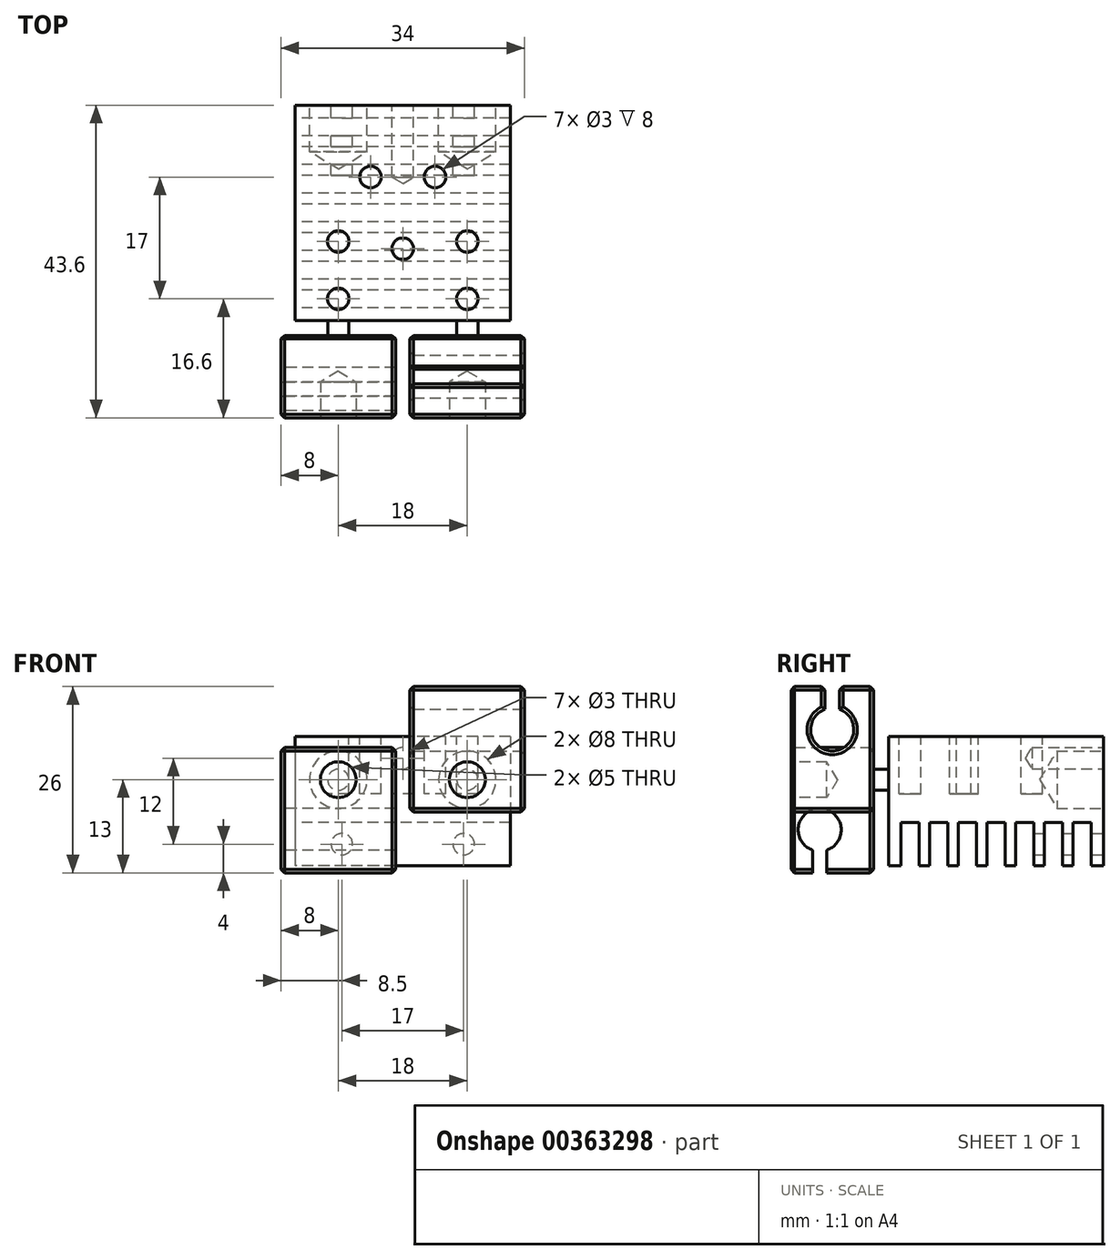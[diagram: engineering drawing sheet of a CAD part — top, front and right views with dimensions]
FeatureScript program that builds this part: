
annotation { "Feature Type Name" : "Feature", "Feature Type Description" : "" }
export const myFeature = defineFeature(function(context is Context, id is Id, definition is map)
    precondition{}
    {
        {
            var Q0;
            Q0=qCreatedBy(makeId("Top.planeOp"),FACE);
            var sketch = newSketch(context, id + "F0", { "sketchPlane" : qUnion([Q0])});
            skLineSegment(sketch, "E0.bottom", {"start": v(15, -15) * mm, "end": v(-15, -15) * mm});
            skLineSegment(sketch, "E0.top", {"start": v(15, 15) * mm, "end": v(-15, 15) * mm});
            skLineSegment(sketch, "E0.left", {"start": v(15, -15) * mm, "end": v(15, 15) * mm});
            skLineSegment(sketch, "E0.right", {"start": v(-15, -15) * mm, "end": v(-15, 15) * mm});
            skPoint(sketch, "E0.middle", {"position": v(0, 0) * mm});
            skSolve(sketch);
        }
        {
            var Q0;
            Q0=makeQuery(id+"F0.imprint","IMPRINT",FACE,{"disambiguationData":[TD([[makeQuery(id+"F0.imprint","IMPRINT",EDGE,{"derivedFrom":sQuery(id+"F0.wireOp",EDGE,"E0.bottom")}),-1.0]])]});
            extrude(context, id + "F11", {"entities" : qUnion([Q0]), "depth" : 18 * mm});
        }
        {
            var Q0;
            Q0=makeQuery(id+"F11.opExtrude","SWEPT_FACE",FACE,{"disambiguationData":[OSD([sQuery(id+"F0.wireOp",EDGE,"E0.top")])]});
            var sketch = newSketch(context, id + "F12", { "sketchPlane" : qUnion([Q0])});
            skPoint(sketch, "E1", {"position": v(-8.5, 3) * mm});
            skPoint(sketch, "E2", {"position": v(8.5, 3) * mm});
            skPoint(sketch, "E3", {"position": v(-9, 12) * mm});
            skPoint(sketch, "E4", {"position": v(9, 12) * mm});
            skPoint(sketch, "E5", {"position": v(0, 15) * mm});
            skSolve(sketch);
        }
        {
            var Q0;
            Q0=sQuery(id+"F12.wireOp",VERTEX,"E3");
            var Q1;
            Q1=sQuery(id+"F12.wireOp",VERTEX,"E4");
            var Q2;
            Q2=makeQuery(id+"F11.opExtrude","SWEPT_BODY",BODY,{"disambiguationData":[OSD([sQuery(id+"F0.wireOp",EDGE,"E0.bottom"),sQuery(id+"F0.wireOp",EDGE,"E0.top"),sQuery(id+"F0.wireOp",EDGE,"E0.left"),sQuery(id+"F0.wireOp",EDGE,"E0.right")])]});
            hole(context, id + "F1", {"style" : HoleStyle.SIMPLE, "endStyle" : HoleEndStyle.BLIND, "holeDiameter" : 8 * mm, "holeDepth" : 6.5 * mm, "locations" : qUnion([Q0, Q1]), "scope" : qUnion([Q2]), "tappedDepth" : 12 * mm, "tapClearance" : 3});
        }
        {
            var Q0;
            Q0=makeQuery(id+"F11.opExtrude","CAP_FACE",FACE,{"disambiguationData":[OSD([sQuery(id+"F0.wireOp",EDGE,"E0.bottom"),sQuery(id+"F0.wireOp",EDGE,"E0.top"),sQuery(id+"F0.wireOp",EDGE,"E0.left"),sQuery(id+"F0.wireOp",EDGE,"E0.right")])],"isStart":true});
            var sketch = newSketch(context, id + "F13", { "sketchPlane" : qUnion([Q0])});
            skLineSegment(sketch, "E6.bottom", {"start": v(15, -13.25) * mm, "end": v(-15.01, -13.25) * mm});
            skLineSegment(sketch, "E6.top", {"start": v(15, -10.75) * mm, "end": v(-15.01, -10.75) * mm});
            skLineSegment(sketch, "E6.left", {"start": v(15, -13.25) * mm, "end": v(15, -10.75) * mm});
            skLineSegment(sketch, "E6.right", {"start": v(-15.01, -13.25) * mm, "end": v(-15.01, -10.75) * mm});
            skLineSegment(sketch, "E7.0.1.0", {"start": v(15, -9.25) * mm, "end": v(15, -6.75) * mm});
            skLineSegment(sketch, "E7.0.1.1", {"start": v(-15.01, -9.25) * mm, "end": v(-15.01, -6.75) * mm});
            skLineSegment(sketch, "E7.0.1.2", {"start": v(15, -9.25) * mm, "end": v(-15.01, -9.25) * mm});
            skLineSegment(sketch, "E7.0.1.3", {"start": v(15, -6.75) * mm, "end": v(-15.01, -6.75) * mm});
            skLineSegment(sketch, "E7.0.2.0", {"start": v(15, -5.25) * mm, "end": v(15, -2.75) * mm});
            skLineSegment(sketch, "E7.0.2.1", {"start": v(-15.01, -5.25) * mm, "end": v(-15.01, -2.75) * mm});
            skLineSegment(sketch, "E7.0.2.2", {"start": v(15, -5.25) * mm, "end": v(-15.01, -5.25) * mm});
            skLineSegment(sketch, "E7.0.2.3", {"start": v(15, -2.75) * mm, "end": v(-15.01, -2.75) * mm});
            skLineSegment(sketch, "E7.0.3.0", {"start": v(15, -1.25) * mm, "end": v(15, 1.25) * mm});
            skLineSegment(sketch, "E7.0.3.1", {"start": v(-15.01, -1.25) * mm, "end": v(-15.01, 1.25) * mm});
            skLineSegment(sketch, "E7.0.3.2", {"start": v(15, -1.25) * mm, "end": v(-15.01, -1.25) * mm});
            skLineSegment(sketch, "E7.0.3.3", {"start": v(15, 1.25) * mm, "end": v(-15.01, 1.25) * mm});
            skLineSegment(sketch, "E7.0.4.0", {"start": v(15, 2.75) * mm, "end": v(15, 5.25) * mm});
            skLineSegment(sketch, "E7.0.4.1", {"start": v(-15.01, 2.75) * mm, "end": v(-15.01, 5.25) * mm});
            skLineSegment(sketch, "E7.0.4.2", {"start": v(15, 2.75) * mm, "end": v(-15.01, 2.75) * mm});
            skLineSegment(sketch, "E7.0.4.3", {"start": v(15, 5.25) * mm, "end": v(-15.01, 5.25) * mm});
            skLineSegment(sketch, "E7.0.5.0", {"start": v(15, 6.75) * mm, "end": v(15, 9.25) * mm});
            skLineSegment(sketch, "E7.0.5.1", {"start": v(-15.01, 6.75) * mm, "end": v(-15.01, 9.25) * mm});
            skLineSegment(sketch, "E7.0.5.2", {"start": v(15, 6.75) * mm, "end": v(-15.01, 6.75) * mm});
            skLineSegment(sketch, "E7.0.5.3", {"start": v(15, 9.25) * mm, "end": v(-15.01, 9.25) * mm});
            skLineSegment(sketch, "E7.0.6.0", {"start": v(15, 10.75) * mm, "end": v(15, 13.25) * mm});
            skLineSegment(sketch, "E7.0.6.1", {"start": v(-15.01, 10.75) * mm, "end": v(-15.01, 13.25) * mm});
            skLineSegment(sketch, "E7.0.6.2", {"start": v(15, 10.75) * mm, "end": v(-15.01, 10.75) * mm});
            skLineSegment(sketch, "E7.0.6.3", {"start": v(15, 13.25) * mm, "end": v(-15.01, 13.25) * mm});
            skLineSegment(sketch, "E7.direction1", {"start": v(-15.01, -13.25) * mm, "end": v(9.99, -13.25) * mm, "construction": true});
            skLineSegment(sketch, "E7.direction2", {"start": v(-15.01, -13.25) * mm, "end": v(-15.01, -9.25) * mm, "construction": true});
            skSolve(sketch);
        }
        {
            var Q0;
            {var subQ0=sQuery(id+"F13.wireOp",EDGE,"E7.0.6.0");Q0=makeQuery(id+"F13.imprint","IMPRINT",FACE,{"disambiguationData":[TD([[makeQuery(id+"F13.imprint","IMPRINT",EDGE,{"derivedFrom":subQ0}),-1.0]])]});}
            var Q1;
            {var subQ0=sQuery(id+"F13.wireOp",EDGE,"E7.0.5.0");Q1=makeQuery(id+"F13.imprint","IMPRINT",FACE,{"disambiguationData":[TD([[makeQuery(id+"F13.imprint","IMPRINT",EDGE,{"derivedFrom":subQ0}),-1.0]])]});}
            var Q2;
            {var subQ0=sQuery(id+"F13.wireOp",EDGE,"E7.0.4.0");Q2=makeQuery(id+"F13.imprint","IMPRINT",FACE,{"disambiguationData":[TD([[makeQuery(id+"F13.imprint","IMPRINT",EDGE,{"derivedFrom":subQ0}),-1.0]])]});}
            var Q3;
            {var subQ0=sQuery(id+"F13.wireOp",EDGE,"E7.0.3.0");Q3=makeQuery(id+"F13.imprint","IMPRINT",FACE,{"disambiguationData":[TD([[makeQuery(id+"F13.imprint","IMPRINT",EDGE,{"derivedFrom":subQ0}),-1.0]])]});}
            var Q4;
            {var subQ0=sQuery(id+"F13.wireOp",EDGE,"E7.0.2.0");Q4=makeQuery(id+"F13.imprint","IMPRINT",FACE,{"disambiguationData":[TD([[makeQuery(id+"F13.imprint","IMPRINT",EDGE,{"derivedFrom":subQ0}),-1.0]])]});}
            var Q5;
            {var subQ0=sQuery(id+"F13.wireOp",EDGE,"E7.0.1.0");Q5=makeQuery(id+"F13.imprint","IMPRINT",FACE,{"disambiguationData":[TD([[makeQuery(id+"F13.imprint","IMPRINT",EDGE,{"derivedFrom":subQ0}),-1.0]])]});}
            var Q6;
            {var subQ0=sQuery(id+"F13.wireOp",EDGE,"E6.left");Q6=makeQuery(id+"F13.imprint","IMPRINT",FACE,{"disambiguationData":[TD([[makeQuery(id+"F13.imprint","IMPRINT",EDGE,{"derivedFrom":subQ0}),-1.0]])]});}
            extrude(context, id + "F14", {"entities" : qUnion([Q0, Q1, Q2, Q3, Q4, Q5, Q6]), "operationType" : NewBodyOperationType.REMOVE, "oppositeDirection" : true, "depth" : 6 * mm});
        }
        {
            var Q0;
            Q0=sQuery(id+"F12.wireOp",VERTEX,"E2");
            var Q1;
            Q1=sQuery(id+"F12.wireOp",VERTEX,"E1");
            var Q2;
            Q2=sQuery(id+"F12.wireOp",VERTEX,"E5");
            var Q3;
            Q3=makeQuery(id+"F11.opExtrude","SWEPT_BODY",BODY,{"disambiguationData":[OSD([sQuery(id+"F0.wireOp",EDGE,"E0.bottom"),sQuery(id+"F0.wireOp",EDGE,"E0.top"),sQuery(id+"F0.wireOp",EDGE,"E0.left"),sQuery(id+"F0.wireOp",EDGE,"E0.right")])]});
            hole(context, id + "F15", {"style" : HoleStyle.SIMPLE, "endStyle" : HoleEndStyle.BLIND, "holeDiameter" : 3 * mm, "holeDepth" : 10 * mm, "locations" : qUnion([Q0, Q1, Q2]), "scope" : qUnion([Q3])});
        }
        {
            var Q0;
            Q0=makeQuery(id+"F11.opExtrude","SWEPT_FACE",FACE,{"disambiguationData":[OSD([sQuery(id+"F0.wireOp",EDGE,"E0.bottom")])]});
            var sketch = newSketch(context, id + "F2", { "sketchPlane" : qUnion([Q0])});
            skCircle(sketch, "E8", {"center": v(9, 12) * mm, "radius": 1.48 * mm});
            skCircle(sketch, "E9", {"center": v(-9, 12) * mm, "radius": 1.48 * mm});
            skLineSegment(sketch, "E10", {"start": v(-15, 12) * mm, "end": v(15, 12) * mm, "construction": true});
            skSolve(sketch);
        }
        {
            var Q0;
            Q0=makeQuery(id+"F2.imprint","IMPRINT",FACE,{"disambiguationData":[TD([[makeQuery(id+"F2.imprint","IMPRINT",EDGE,{"derivedFrom":sQuery(id+"F2.wireOp",EDGE,"E9")}),1.0]])]});
            var Q1;
            Q1=makeQuery(id+"F2.imprint","IMPRINT",FACE,{"disambiguationData":[TD([[makeQuery(id+"F2.imprint","IMPRINT",EDGE,{"derivedFrom":sQuery(id+"F2.wireOp",EDGE,"E8")}),1.0]])]});
            extrude(context, id + "F3", {"entities" : qUnion([Q0, Q1]), "operationType" : NewBodyOperationType.ADD, "depth" : 2.1 * mm});
        }
        {
            var Q0;
            Q0=makeQuery(id+"F3.opExtrude","CAP_FACE",FACE,{"disambiguationData":[OSD([sQuery(id+"F2.wireOp",EDGE,"E8")])],"isStart":false});
            var sketch = newSketch(context, id + "F16", { "sketchPlane" : qUnion([Q0])});
            skLineSegment(sketch, "E11.bottom", {"start": v(1, 25) * mm, "end": v(17, 25) * mm});
            skLineSegment(sketch, "E11.top", {"start": v(1, 7.5) * mm, "end": v(17, 7.5) * mm});
            skLineSegment(sketch, "E11.left", {"start": v(1, 25) * mm, "end": v(1, 7.5) * mm});
            skLineSegment(sketch, "E11.right", {"start": v(17, 25) * mm, "end": v(17, 7.5) * mm});
            skPoint(sketch, "E12", {"position": v(9, 12) * mm});
            skSolve(sketch);
        }
        {
            var Q0;
            Q0=makeQuery(id+"F3.opExtrude","CAP_FACE",FACE,{"disambiguationData":[OSD([sQuery(id+"F2.wireOp",EDGE,"E9")])],"isStart":false});
            var sketch = newSketch(context, id + "F17", { "sketchPlane" : qUnion([Q0])});
            skPoint(sketch, "E13", {"position": v(-9, 12) * mm});
            skLineSegment(sketch, "E14.bottom", {"start": v(-17, 16.5) * mm, "end": v(-1, 16.5) * mm});
            skLineSegment(sketch, "E14.top", {"start": v(-17, -1) * mm, "end": v(-1, -1) * mm});
            skLineSegment(sketch, "E14.left", {"start": v(-17, 16.5) * mm, "end": v(-17, -1) * mm});
            skLineSegment(sketch, "E14.right", {"start": v(-1, 16.5) * mm, "end": v(-1, -1) * mm});
            skSolve(sketch);
        }
        {
            var Q0;
            Q0=qSketchRegion(id+"F17",true);
            var Q1;
            Q1=qSketchRegion(id+"F16",true);
            extrude(context, id + "F18", {"entities" : qUnion([Q0, Q1]), "operationType" : NewBodyOperationType.ADD, "depth" : 11.5 * mm});
        }
        {
            var Q0;
            Q0=makeQuery(id+"F18.opExtrude","CAP_FACE",FACE,{"disambiguationData":[OSD([sQuery(id+"F16.wireOp",EDGE,"E11.bottom"),sQuery(id+"F16.wireOp",EDGE,"E11.top"),sQuery(id+"F16.wireOp",EDGE,"E11.left"),sQuery(id+"F16.wireOp",EDGE,"E11.right")])],"isStart":false});
            var sketch = newSketch(context, id + "F19", { "sketchPlane" : qUnion([Q0])});
            skPoint(sketch, "E15", {"position": v(9, 12) * mm});
            skPoint(sketch, "E15.positionSnap0", {"position": v(9, 7.5) * mm});
            skSolve(sketch);
        }
        {
            var Q0;
            Q0=makeQuery(id+"F18.opExtrude","CAP_FACE",FACE,{"disambiguationData":[OSD([sQuery(id+"F17.wireOp",EDGE,"E14.bottom"),sQuery(id+"F17.wireOp",EDGE,"E14.top"),sQuery(id+"F17.wireOp",EDGE,"E14.left"),sQuery(id+"F17.wireOp",EDGE,"E14.right")])],"isStart":false});
            var sketch = newSketch(context, id + "F20", { "sketchPlane" : qUnion([Q0])});
            skPoint(sketch, "E16", {"position": v(-9, 12) * mm});
            skPoint(sketch, "E16.positionSnap0", {"position": v(-9, 16.5) * mm});
            skSolve(sketch);
        }
        {
            var Q0;
            Q0=sQuery(id+"F20.wireOp",VERTEX,"E16");
            var Q1;
            Q1=sQuery(id+"F19.wireOp",VERTEX,"E15");
            var Q2;
            Q2=makeQuery(id+"F11.opExtrude","SWEPT_BODY",BODY,{"disambiguationData":[OSD([sQuery(id+"F0.wireOp",EDGE,"E0.bottom"),sQuery(id+"F0.wireOp",EDGE,"E0.top"),sQuery(id+"F0.wireOp",EDGE,"E0.left"),sQuery(id+"F0.wireOp",EDGE,"E0.right")])]});
            hole(context, id + "F4", {"style" : HoleStyle.SIMPLE, "endStyle" : HoleEndStyle.BLIND, "holeDiameter" : 5 * mm, "holeDepth" : 5 * mm, "locations" : qUnion([Q0, Q1]), "scope" : qUnion([Q2]), "tappedDepth" : 12 * mm, "tapClearance" : 3});
        }
        {
            var Q0;
            Q0=makeQuery(id+"F18.opExtrude","SWEPT_FACE",FACE,{"disambiguationData":[OSD([sQuery(id+"F16.wireOp",EDGE,"E11.right")])]});
            var sketch = newSketch(context, id + "F5", { "sketchPlane" : qUnion([Q0])});
            skArc(sketch, "E17", {"start": v(-23.85, 21.83) * mm, "mid": v(-22.85, 16) * mm, "end": v(-21.85, 21.83) * mm});
            skLineSegment(sketch, "E18.bottom", {"start": v(-23.85, 25) * mm, "end": v(-21.85, 25) * mm});
            skLineSegment(sketch, "E18.left", {"start": v(-23.85, 25) * mm, "end": v(-23.85, 21.83) * mm});
            skLineSegment(sketch, "E18.right", {"start": v(-21.85, 25) * mm, "end": v(-21.85, 21.83) * mm});
            skLineSegment(sketch, "E19", {"start": v(-22.85, 19) * mm, "end": v(-22.85, 25) * mm, "construction": true});
            skSolve(sketch);
        }
        {
            var Q0;
            {var subQ0=sQuery(id+"F5.wireOp",EDGE,"E17");Q0=makeQuery(id+"F5.imprint","IMPRINT",FACE,{"disambiguationData":[TD([[makeQuery(id+"F5.imprint","IMPRINT",EDGE,{"derivedFrom":subQ0}),1.0]])]});}
            extrude(context, id + "F6", {"entities" : qUnion([Q0]), "operationType" : NewBodyOperationType.REMOVE, "endBound" : BoundingType.UP_TO_NEXT, "oppositeDirection" : true, "depth" : 25 * mm});
        }
        {
            var Q0;
            Q0=makeQuery(id+"F18.opExtrude","SWEPT_FACE",FACE,{"disambiguationData":[OSD([sQuery(id+"F16.wireOp",EDGE,"E11.right")])]});
            var Q1;
            Q1=makeQuery(id+"F18.opExtrude","SWEPT_FACE",FACE,{"disambiguationData":[OSD([sQuery(id+"F16.wireOp",EDGE,"E11.top")])]});
            var Q2;
            Q2=makeQuery(id+"F18.opExtrude","SWEPT_FACE",FACE,{"disambiguationData":[OSD([sQuery(id+"F17.wireOp",EDGE,"E14.top")])]});
            var Q3;
            Q3=makeQuery(id+"F18.opExtrude","SWEPT_FACE",FACE,{"disambiguationData":[OSD([sQuery(id+"F17.wireOp",EDGE,"E14.right")])]});
            var Q4;
            {var subQ2=sQuery(id+"F16.wireOp",EDGE,"E11.bottom");Q4=makeQuery(id+"F6.boolean.opBoolean","SPLIT",FACE,{"disambiguationData":[TD([makeQuery(id+"F6.opExtrude","SWEPT_FACE",FACE,{"disambiguationData":[OSD([sQuery(id+"F5.wireOp",EDGE,"E18.right")])]})])],"derivedFrom":makeQuery(id+"F18.opExtrude","SWEPT_FACE",FACE,{"disambiguationData":[OSD([subQ2])]})});}
            var Q5;
            {var subQ2=sQuery(id+"F16.wireOp",EDGE,"E11.bottom");Q5=makeQuery(id+"F6.boolean.opBoolean","SPLIT",FACE,{"disambiguationData":[TD([makeQuery(id+"F6.opExtrude","SWEPT_FACE",FACE,{"disambiguationData":[OSD([sQuery(id+"F5.wireOp",EDGE,"E18.left")])]})])],"derivedFrom":makeQuery(id+"F18.opExtrude","SWEPT_FACE",FACE,{"disambiguationData":[OSD([subQ2])]})});}
            var Q6;
            Q6=makeQuery(id+"F18.opExtrude","SWEPT_FACE",FACE,{"disambiguationData":[OSD([sQuery(id+"F17.wireOp",EDGE,"E14.bottom")])]});
            var Q7;
            Q7=makeQuery(id+"F18.opExtrude","SWEPT_FACE",FACE,{"disambiguationData":[OSD([sQuery(id+"F17.wireOp",EDGE,"E14.left")])]});
            var Q8;
            Q8=makeQuery(id+"F18.opExtrude","SWEPT_FACE",FACE,{"disambiguationData":[OSD([sQuery(id+"F16.wireOp",EDGE,"E11.left")])]});
            chamfer(context, id + "F7", {"entities" : qUnion([Q0, Q1, Q2, Q3, Q4, Q5, Q6, Q7, Q8]), "width" : 0.5 * mm, "tangentPropagation" : true});
        }
        {
            var Q0;
            Q0=makeQuery(id+"F18.opExtrude","SWEPT_FACE",FACE,{"disambiguationData":[OSD([sQuery(id+"F17.wireOp",EDGE,"E14.left")])]});
            var sketch = newSketch(context, id + "F8", { "sketchPlane" : qUnion([Q0])});
            skArc(sketch, "E20", {"start": v(25.6, 2.17) * mm, "mid": v(24.6, 8) * mm, "end": v(23.6, 2.17) * mm});
            skLineSegment(sketch, "E21.top", {"start": v(25.6, -1.5) * mm, "end": v(23.6, -1.5) * mm});
            skLineSegment(sketch, "E21.left", {"start": v(25.6, 11.5) * mm, "end": v(25.6, 7.83) * mm});
            skLineSegment(sketch, "E21.right", {"start": v(23.6, 2.17) * mm, "end": v(23.6, -1.5) * mm});
            skPoint(sketch, "E22.orphan", {"position": v(23.6, 11.5) * mm});
            skLineSegment(sketch, "E23.trimOffspring", {"start": v(25.6, 2.17) * mm, "end": v(25.6, -1.5) * mm});
            skSolve(sketch);
        }
        {
            var Q0;
            {var subQ1=sQuery(id+"F8.wireOp",EDGE,"E20");var subQ9=makeQuery(id+"F8.imprint","IMPRINT",VERTEX,{"derivedFrom":subQ1});Q0=makeQuery(id+"F8.imprint","IMPRINT",FACE,{"disambiguationData":[TD([[makeQuery(id+"F8.imprint","IMPRINT",EDGE,{"disambiguationData":[TD([[subQ9,1.0]])],"derivedFrom":subQ1}),1.0]])]});}
            var Q1;
            {var subQ0=sQuery(id+"F8.wireOp",EDGE,"E21.top");Q1=makeQuery(id+"F8.imprint","IMPRINT",FACE,{"disambiguationData":[TD([[makeQuery(id+"F8.imprint","IMPRINT",EDGE,{"derivedFrom":subQ0}),-1.0]])]});}
            extrude(context, id + "F21", {"entities" : qUnion([Q0, Q1]), "operationType" : NewBodyOperationType.REMOVE, "endBound" : BoundingType.UP_TO_NEXT, "oppositeDirection" : true, "depth" : 25 * mm});
        }
        {
            var Q0;
            Q0=makeQuery(id+"F11.opExtrude","CAP_FACE",FACE,{"disambiguationData":[OSD([sQuery(id+"F0.wireOp",EDGE,"E0.bottom"),sQuery(id+"F0.wireOp",EDGE,"E0.top"),sQuery(id+"F0.wireOp",EDGE,"E0.left"),sQuery(id+"F0.wireOp",EDGE,"E0.right")])],"isStart":false});
            var sketch = newSketch(context, id + "F9", { "sketchPlane" : qUnion([Q0])});
            skLineSegment(sketch, "E24", {"start": v(-15, -12) * mm, "end": v(15, -12) * mm, "construction": true});
            skLineSegment(sketch, "E25", {"start": v(-15, -4) * mm, "end": v(15, -4) * mm, "construction": true});
            skLineSegment(sketch, "E26", {"start": v(-15, 5) * mm, "end": v(15, 5) * mm, "construction": true});
            skLineSegment(sketch, "E27", {"start": v(-15, -5) * mm, "end": v(15, -5) * mm, "construction": true});
            skLineSegment(sketch, "E28", {"start": v(0, -15) * mm, "end": v(0, 15) * mm, "construction": true});
            skCircle(sketch, "E29", {"center": v(0, -5) * mm, "radius": 1.5 * mm});
            skCircle(sketch, "E30", {"center": v(-4.5, 5) * mm, "radius": 1.5 * mm});
            skCircle(sketch, "E31", {"center": v(4.5, 5) * mm, "radius": 1.5 * mm});
            skCircle(sketch, "E32", {"center": v(-9, -12) * mm, "radius": 1.5 * mm});
            skCircle(sketch, "E33", {"center": v(-9, -4) * mm, "radius": 1.5 * mm});
            skCircle(sketch, "E34", {"center": v(9, -12) * mm, "radius": 1.5 * mm});
            skCircle(sketch, "E35", {"center": v(9, -4) * mm, "radius": 1.5 * mm});
            skSolve(sketch);
        }
        {
            var Q0;
            Q0=makeQuery(id+"F9.imprint","IMPRINT",FACE,{"disambiguationData":[TD([[makeQuery(id+"F9.imprint","IMPRINT",EDGE,{"derivedFrom":sQuery(id+"F9.wireOp",EDGE,"E32")}),1.0]])]});
            var Q1;
            Q1=makeQuery(id+"F9.imprint","IMPRINT",FACE,{"disambiguationData":[TD([[makeQuery(id+"F9.imprint","IMPRINT",EDGE,{"derivedFrom":sQuery(id+"F9.wireOp",EDGE,"E33")}),1.0]])]});
            var Q2;
            Q2=makeQuery(id+"F9.imprint","IMPRINT",FACE,{"disambiguationData":[TD([[makeQuery(id+"F9.imprint","IMPRINT",EDGE,{"derivedFrom":sQuery(id+"F9.wireOp",EDGE,"E29")}),1.0]])]});
            var Q3;
            Q3=makeQuery(id+"F9.imprint","IMPRINT",FACE,{"disambiguationData":[TD([[makeQuery(id+"F9.imprint","IMPRINT",EDGE,{"derivedFrom":sQuery(id+"F9.wireOp",EDGE,"E31")}),1.0]])]});
            var Q4;
            Q4=makeQuery(id+"F9.imprint","IMPRINT",FACE,{"disambiguationData":[TD([[makeQuery(id+"F9.imprint","IMPRINT",EDGE,{"derivedFrom":sQuery(id+"F9.wireOp",EDGE,"E35")}),1.0]])]});
            var Q5;
            Q5=makeQuery(id+"F9.imprint","IMPRINT",FACE,{"disambiguationData":[TD([[makeQuery(id+"F9.imprint","IMPRINT",EDGE,{"derivedFrom":sQuery(id+"F9.wireOp",EDGE,"E34")}),1.0]])]});
            var Q6;
            Q6=makeQuery(id+"F9.imprint","IMPRINT",FACE,{"disambiguationData":[TD([[makeQuery(id+"F9.imprint","IMPRINT",EDGE,{"derivedFrom":sQuery(id+"F9.wireOp",EDGE,"E30")}),1.0]])]});
            extrude(context, id + "F10", {"entities" : qUnion([Q0, Q1, Q2, Q3, Q4, Q5, Q6]), "operationType" : NewBodyOperationType.REMOVE, "oppositeDirection" : true, "depth" : 8 * mm});
        }
    });
